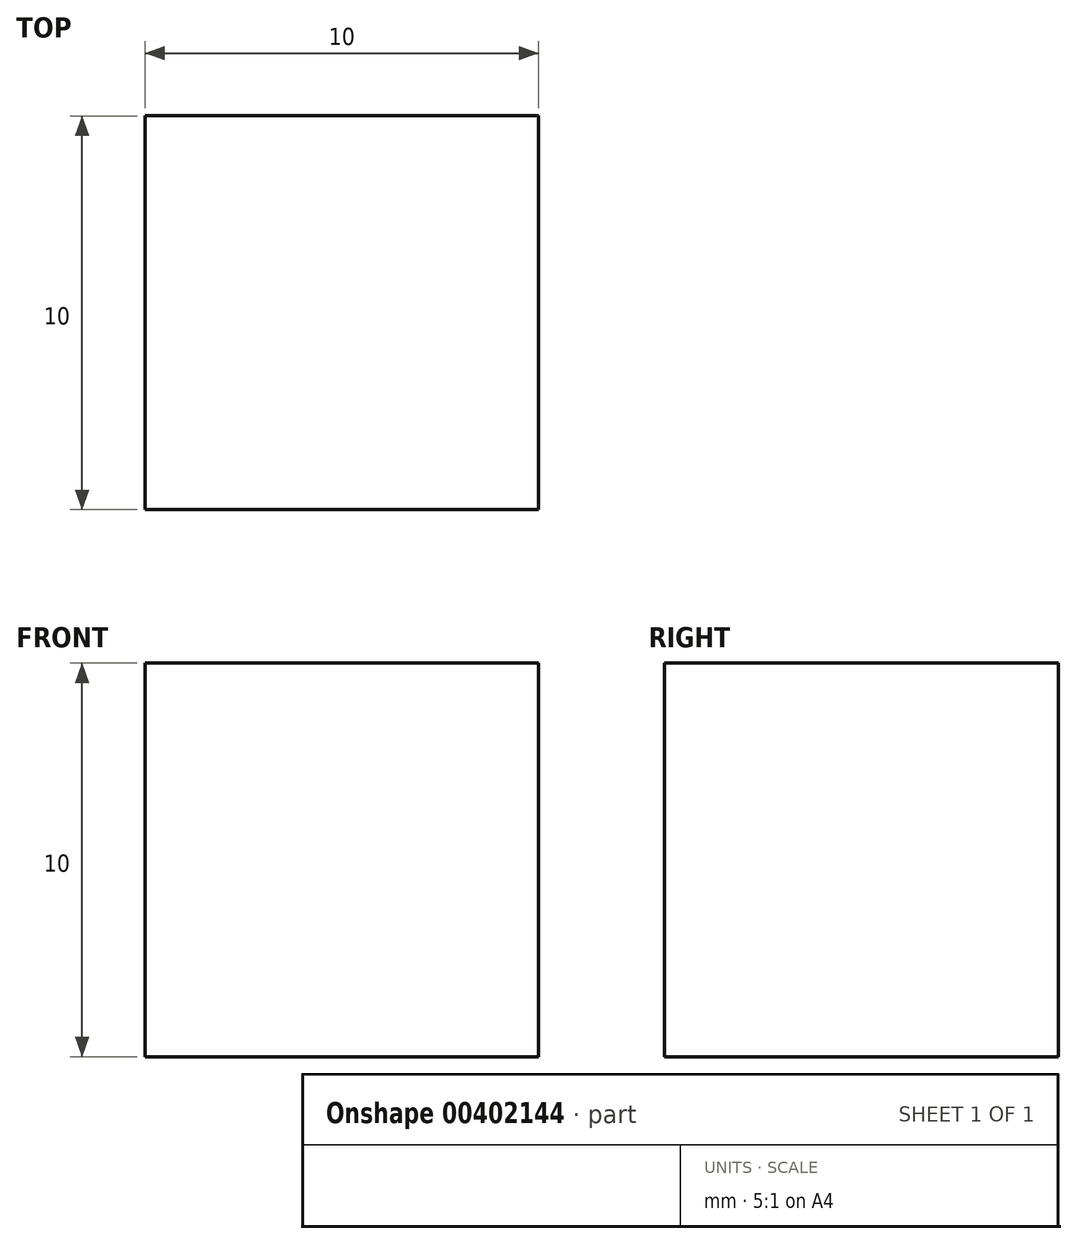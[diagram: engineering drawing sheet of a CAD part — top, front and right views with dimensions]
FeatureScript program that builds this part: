
annotation { "Feature Type Name" : "Feature", "Feature Type Description" : "" }
export const myFeature = defineFeature(function(context is Context, id is Id, definition is map)
    precondition{}
    {
        {
            var Q0;
            Q0=qCreatedBy(makeId("Top.planeOp"),FACE);
            var sketch = newSketch(context, id + "F0", { "sketchPlane" : qUnion([Q0])});
            skLineSegment(sketch, "E0.bottom", {"start": v(-3.54, -6.97) * mm, "end": v(6.46, -6.97) * mm});
            skLineSegment(sketch, "E0.top", {"start": v(-3.54, -16.97) * mm, "end": v(6.46, -16.97) * mm});
            skLineSegment(sketch, "E0.left", {"start": v(-3.54, -6.97) * mm, "end": v(-3.54, -16.97) * mm});
            skLineSegment(sketch, "E0.right", {"start": v(6.46, -6.97) * mm, "end": v(6.46, -16.97) * mm});
            skSolve(sketch);
        }
        {
            var Q0;
            Q0 = qSketchRegion(id + "F0", true);
            extrude(context, id + "F1", {"entities" : qUnion([Q0]), "depth" : 10 * mm});
        }
    });
